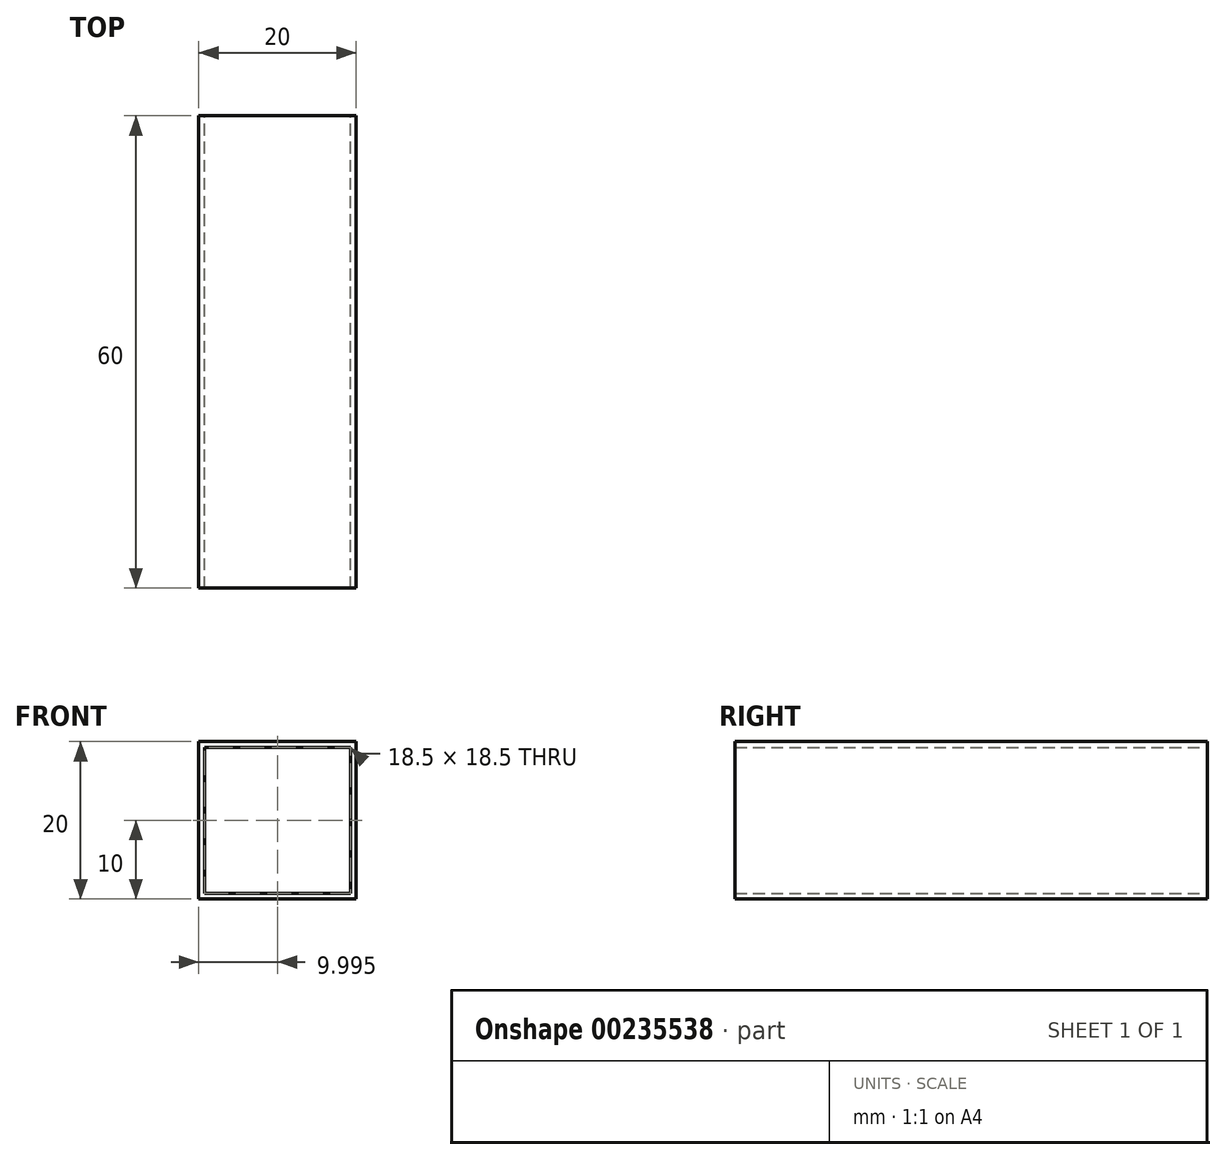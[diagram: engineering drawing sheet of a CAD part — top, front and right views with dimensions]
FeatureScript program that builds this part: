
annotation { "Feature Type Name" : "Feature", "Feature Type Description" : "" }
export const myFeature = defineFeature(function(context is Context, id is Id, definition is map)
    precondition{}
    {
        {
            var Q0;
            Q0=qCreatedBy(makeId("Front.planeOp"),FACE);
            var sketch = newSketch(context, id + "F0", { "sketchPlane" : qUnion([Q0])});
            skLineSegment(sketch, "E0.bottom", {"start": v(-34.48, 27) * mm, "end": v(-54.48, 27) * mm});
            skLineSegment(sketch, "E0.top", {"start": v(-34.48, 47) * mm, "end": v(-54.48, 47) * mm});
            skLineSegment(sketch, "E0.left", {"start": v(-34.48, 27) * mm, "end": v(-34.48, 47) * mm});
            skLineSegment(sketch, "E0.right", {"start": v(-54.48, 27) * mm, "end": v(-54.48, 47) * mm});
            skPoint(sketch, "E0.middle", {"position": v(-44.48, 37) * mm});
            skLineSegment(sketch, "E1.bottom", {"start": v(-35.23, 27.75) * mm, "end": v(-53.73, 27.75) * mm});
            skLineSegment(sketch, "E1.top", {"start": v(-35.23, 46.25) * mm, "end": v(-53.73, 46.25) * mm});
            skLineSegment(sketch, "E1.left", {"start": v(-35.23, 27.75) * mm, "end": v(-35.23, 46.25) * mm});
            skLineSegment(sketch, "E1.right", {"start": v(-53.73, 27.75) * mm, "end": v(-53.73, 46.25) * mm});
            skSolve(sketch);
        }
        {
            var Q0;
            Q0=makeQuery(id+"F0.imprint","IMPRINT",FACE,{"disambiguationData":[TD([[makeQuery(id+"F0.imprint","IMPRINT",EDGE,{"derivedFrom":sQuery(id+"F0.wireOp",EDGE,"E0.bottom")}),-1.0]])]});
            extrude(context, id + "F1", {"entities" : qUnion([Q0]), "depth" : 60 * mm});
        }
    });
